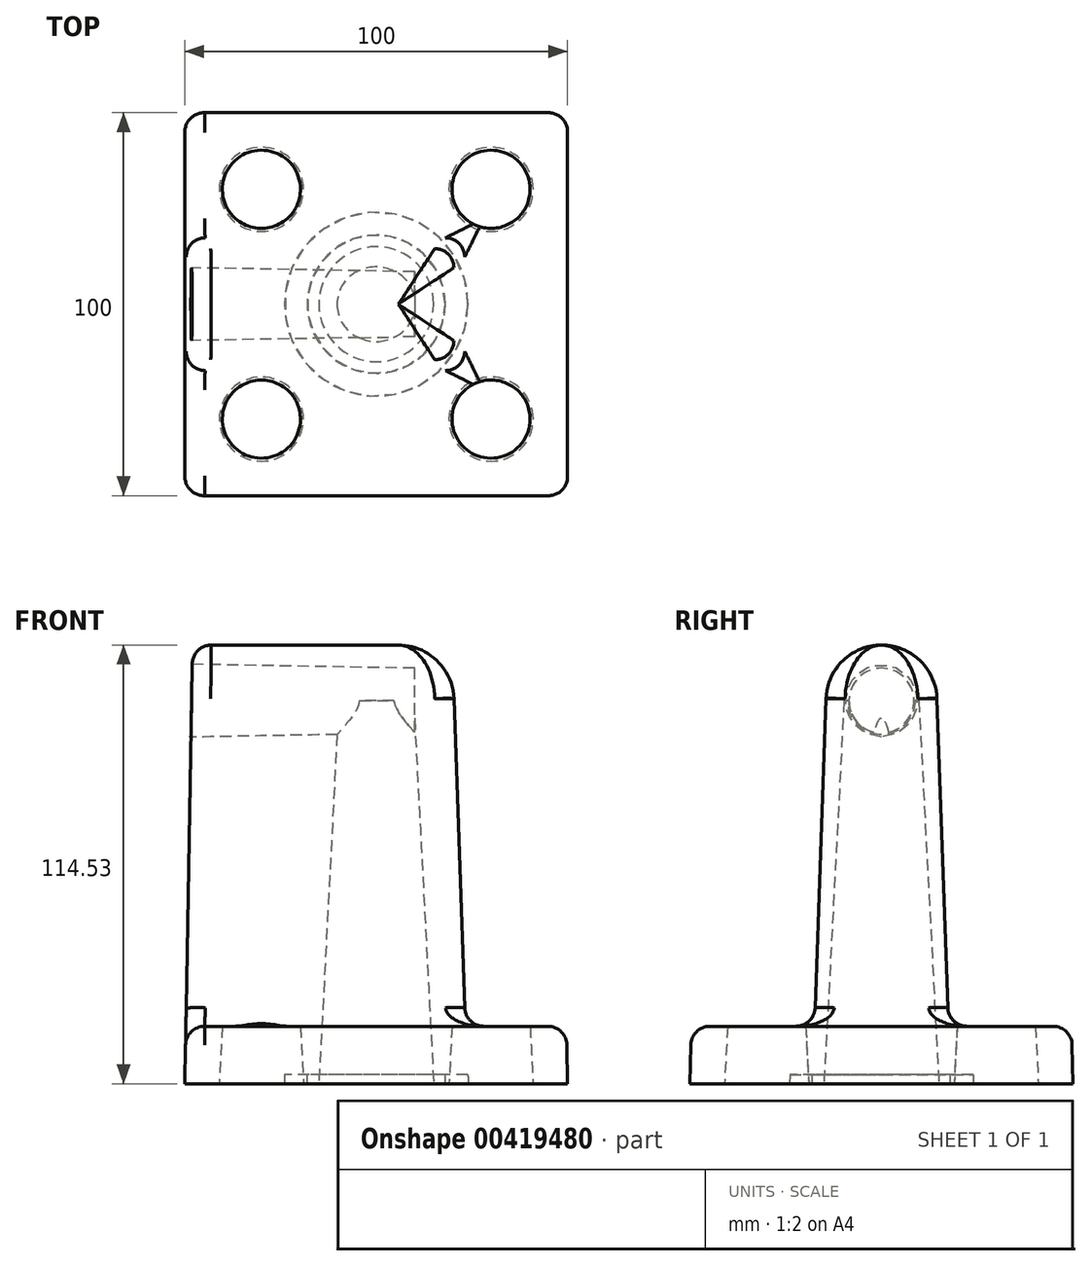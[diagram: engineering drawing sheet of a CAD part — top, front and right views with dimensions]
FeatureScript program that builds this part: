
annotation { "Feature Type Name" : "Feature", "Feature Type Description" : "" }
export const myFeature = defineFeature(function(context is Context, id is Id, definition is map)
    precondition{}
    {
        {
            var Q0;
            Q0=qCreatedBy(makeId("Top.planeOp"),FACE);
            var sketch = newSketch(context, id + "F0", { "sketchPlane" : qUnion([Q0])});
            skLineSegment(sketch, "E0.bottom", {"start": v(50, 50) * mm, "end": v(-50, 50) * mm});
            skLineSegment(sketch, "E0.top", {"start": v(50, -50) * mm, "end": v(-50, -50) * mm});
            skLineSegment(sketch, "E0.left", {"start": v(50, 50) * mm, "end": v(50, -50) * mm});
            skLineSegment(sketch, "E0.right", {"start": v(-50, 50) * mm, "end": v(-50, -50) * mm});
            skPoint(sketch, "E0.middle", {"position": v(0, 0) * mm});
            skCircle(sketch, "E1", {"center": v(-30, 30) * mm, "radius": 11 * mm});
            skCircle(sketch, "E2", {"center": v(30, 30) * mm, "radius": 11 * mm});
            skCircle(sketch, "E3", {"center": v(30, -30) * mm, "radius": 11 * mm});
            skCircle(sketch, "E4", {"center": v(-30, -30) * mm, "radius": 11 * mm});
            skCircle(sketch, "E5", {"center": v(0, 0) * mm, "radius": 15 * mm});
            skSolve(sketch);
        }
        {
            var Q0;
            Q0=makeQuery(id+"F0.imprint","IMPRINT",FACE,{"disambiguationData":[TD([[makeQuery(id+"F0.imprint","IMPRINT",EDGE,{"derivedFrom":sQuery(id+"F0.wireOp",EDGE,"E5")}),1.0]])]});
            var Q1;
            Q1=makeQuery(id+"F0.imprint","IMPRINT",FACE,{"disambiguationData":[TD([[makeQuery(id+"F0.imprint","IMPRINT",EDGE,{"derivedFrom":sQuery(id+"F0.wireOp",EDGE,"E0.bottom")}),1.0]])]});
            var Q2;
            Q2=makeQuery(id+"F0.imprint","IMPRINT",FACE,{"disambiguationData":[TD([[makeQuery(id+"F0.imprint","IMPRINT",EDGE,{"derivedFrom":sQuery(id+"F0.wireOp",EDGE,"E3")}),1.0]])]});
            var Q3;
            Q3=makeQuery(id+"F0.imprint","IMPRINT",FACE,{"disambiguationData":[TD([[makeQuery(id+"F0.imprint","IMPRINT",EDGE,{"derivedFrom":sQuery(id+"F0.wireOp",EDGE,"E4")}),1.0]])]});
            var Q4;
            Q4=makeQuery(id+"F0.imprint","IMPRINT",FACE,{"disambiguationData":[TD([[makeQuery(id+"F0.imprint","IMPRINT",EDGE,{"derivedFrom":sQuery(id+"F0.wireOp",EDGE,"E2")}),1.0]])]});
            var Q5;
            Q5=makeQuery(id+"F0.imprint","IMPRINT",FACE,{"disambiguationData":[TD([[makeQuery(id+"F0.imprint","IMPRINT",EDGE,{"derivedFrom":sQuery(id+"F0.wireOp",EDGE,"E1")}),1.0]])]});
            extrude(context, id + "F1", {"entities" : qUnion([Q0, Q1, Q2, Q3, Q4, Q5]), "depth" : 150 * mm, "hasDraft" : true, "draftAngle" : 1 * degree, "draftPullDirection" : true});
        }
        {
            var Q0;
            Q0=qCreatedBy(makeId("Right.planeOp"),FACE);
            var Q1;
            Q1=makeQuery(id+"F1.opExtrude","CAP_VERTEX",VERTEX,{"disambiguationData":[OSD([sQuery(id+"F0.wireOp",EDGE,"E0.top"),sQuery(id+"F0.wireOp",EDGE,"E0.right")])],"isStart":true});
            cPlane(context, id + "F2", {"entities" : qUnion([Q0, Q1]), "cplaneType" : CPlaneType.PLANE_POINT, "offset" : 25 * mm, "width" : 150 * mm, "height" : 150 * mm});
        }
        {
            var Q0;
            Q0=qCreatedBy(id+"F2.planeOp",FACE);
            var sketch = newSketch(context, id + "F3", { "sketchPlane" : qUnion([Q0])});
            skLineSegment(sketch, "E6", {"start": v(44.82, 15) * mm, "end": v(22.33, 15) * mm});
            skCircle(sketch, "E7", {"center": v(0, 100) * mm, "radius": 9.53 * mm});
            skArc(sketch, "E8", {"start": v(14.52, 100.5) * mm, "mid": v(10.09, 110.45) * mm, "end": v(0, 114.53) * mm});
            skLineSegment(sketch, "E9", {"start": v(14.52, 100.5) * mm, "end": v(17.33, 19.83) * mm});
            skLineSegment(sketch, "E10", {"start": v(0, 0) * mm, "end": v(0, 100) * mm, "construction": true});
            skLineSegment(sketch, "E11", {"start": v(49.82, 10.09) * mm, "end": v(50, 0) * mm});
            skLineSegment(sketch, "E12", {"start": v(50, 0) * mm, "end": v(65.53, 0) * mm});
            skLineSegment(sketch, "E13", {"start": v(65.53, 0) * mm, "end": v(56.35, 171.03) * mm});
            skLineSegment(sketch, "E14", {"start": v(56.35, 171.03) * mm, "end": v(0, 171.03) * mm});
            skPoint(sketch, "E15.visualSharp", {"position": v(17.5, 15) * mm});
            skArc(sketch, "E15.filletArc", {"start": v(17.33, 19.83) * mm, "mid": v(18.86, 16.4) * mm, "end": v(22.33, 15) * mm});
            skPoint(sketch, "E16.visualSharp", {"position": v(49.74, 15) * mm});
            skArc(sketch, "E16.filletArc", {"start": v(49.82, 10.09) * mm, "mid": v(48.33, 13.57) * mm, "end": v(44.82, 15) * mm});
            skArc(sketch, "E17.MirrorCS", {"start": v(-14.52, 100.5) * mm, "mid": v(-10.09, 110.45) * mm, "end": v(0, 114.53) * mm});
            skLineSegment(sketch, "E18.MirrorCS", {"start": v(-14.52, 100.5) * mm, "end": v(-17.33, 19.83) * mm});
            skArc(sketch, "E19.MirrorCS", {"start": v(-17.33, 19.83) * mm, "mid": v(-18.86, 16.4) * mm, "end": v(-22.33, 15) * mm});
            skLineSegment(sketch, "E20.MirrorCS", {"start": v(-44.82, 15) * mm, "end": v(-22.33, 15) * mm});
            skArc(sketch, "E21.MirrorCS", {"start": v(-49.82, 10.09) * mm, "mid": v(-48.33, 13.57) * mm, "end": v(-44.82, 15) * mm});
            skLineSegment(sketch, "E22.MirrorCS", {"start": v(-49.82, 10.09) * mm, "end": v(-50, 0) * mm});
            skLineSegment(sketch, "E23.MirrorCS", {"start": v(-50, 0) * mm, "end": v(-65.53, 0) * mm});
            skLineSegment(sketch, "E24.MirrorCS", {"start": v(-65.53, 0) * mm, "end": v(-56.35, 171.03) * mm});
            skLineSegment(sketch, "E25.MirrorCS", {"start": v(-56.35, 171.03) * mm, "end": v(0, 171.03) * mm});
            skSolve(sketch);
        }
        {
            var Q0;
            Q0=makeQuery(id+"F3.imprint","IMPRINT",FACE,{"disambiguationData":[TD([[makeQuery(id+"F3.imprint","IMPRINT",EDGE,{"derivedFrom":sQuery(id+"F3.wireOp",EDGE,"E6")}),-1.0]])]});
            extrude(context, id + "F4", {"entities" : qUnion([Q0]), "operationType" : NewBodyOperationType.REMOVE, "endBound" : BoundingType.THROUGH_ALL, "depth" : 25 * mm});
        }
        {
            var Q0;
            Q0=makeQuery(id+"F0.imprint","IMPRINT",FACE,{"disambiguationData":[TD([[makeQuery(id+"F0.imprint","IMPRINT",EDGE,{"derivedFrom":sQuery(id+"F0.wireOp",EDGE,"E5")}),1.0]])]});
            var Q1;
            Q1=makeQuery(id+"F0.imprint","IMPRINT",FACE,{"disambiguationData":[TD([[makeQuery(id+"F0.imprint","IMPRINT",EDGE,{"derivedFrom":sQuery(id+"F0.wireOp",EDGE,"E4")}),1.0]])]});
            var Q2;
            Q2=makeQuery(id+"F0.imprint","IMPRINT",FACE,{"disambiguationData":[TD([[makeQuery(id+"F0.imprint","IMPRINT",EDGE,{"derivedFrom":sQuery(id+"F0.wireOp",EDGE,"E3")}),1.0]])]});
            var Q3;
            Q3=makeQuery(id+"F0.imprint","IMPRINT",FACE,{"disambiguationData":[TD([[makeQuery(id+"F0.imprint","IMPRINT",EDGE,{"derivedFrom":sQuery(id+"F0.wireOp",EDGE,"E2")}),1.0]])]});
            var Q4;
            Q4=makeQuery(id+"F0.imprint","IMPRINT",FACE,{"disambiguationData":[TD([[makeQuery(id+"F0.imprint","IMPRINT",EDGE,{"derivedFrom":sQuery(id+"F0.wireOp",EDGE,"E1")}),1.0]])]});
            extrude(context, id + "F5", {"entities" : qUnion([Q0, Q1, Q2, Q3, Q4]), "operationType" : NewBodyOperationType.REMOVE, "depth" : 100 * mm, "hasDraft" : true, "draftAngle" : 3 * degree, "draftPullDirection" : true});
        }
        {
            var Q0;
            Q0=makeQuery(id+"F3.imprint","IMPRINT",FACE,{"disambiguationData":[TD([[makeQuery(id+"F3.imprint","IMPRINT",EDGE,{"derivedFrom":sQuery(id+"F3.wireOp",EDGE,"E7")}),1.0]])]});
            extrude(context, id + "F6", {"entities" : qUnion([Q0]), "operationType" : NewBodyOperationType.REMOVE, "depth" : 60 * mm, "hasDraft" : true, "draftAngle" : 1 * degree, "draftPullDirection" : true});
        }
        {
            var Q0;
            Q0=qCreatedBy(makeId("Front.planeOp"),FACE);
            var sketch = newSketch(context, id + "F7", { "sketchPlane" : qUnion([Q0])});
            skLineSegment(sketch, "E26", {"start": v(50, 0) * mm, "end": v(49.82, 10.09) * mm});
            skLineSegment(sketch, "E27", {"start": v(44.82, 15) * mm, "end": v(28.1, 15) * mm});
            skLineSegment(sketch, "E28", {"start": v(23.1, 19.83) * mm, "end": v(20.28, 100.53) * mm});
            skLineSegment(sketch, "E29", {"start": v(5.8, 114.53) * mm, "end": v(-54.15, 114.53) * mm});
            skLineSegment(sketch, "E30", {"start": v(-54.15, 114.53) * mm, "end": v(-54.15, 135.79) * mm});
            skLineSegment(sketch, "E31", {"start": v(-54.15, 135.79) * mm, "end": v(70.57, 135.79) * mm});
            skLineSegment(sketch, "E32", {"start": v(70.57, 135.79) * mm, "end": v(70.57, 0) * mm});
            skLineSegment(sketch, "E33", {"start": v(70.57, 0) * mm, "end": v(50, 0) * mm});
            skPoint(sketch, "E34.visualSharp", {"position": v(19.8, 114.53) * mm});
            skArc(sketch, "E34.filletArc", {"start": v(20.28, 100.53) * mm, "mid": v(15.86, 110.46) * mm, "end": v(5.8, 114.53) * mm});
            skPoint(sketch, "E35.visualSharp", {"position": v(23.27, 15) * mm});
            skArc(sketch, "E35.filletArc", {"start": v(23.1, 19.83) * mm, "mid": v(24.63, 16.4) * mm, "end": v(28.1, 15) * mm});
            skPoint(sketch, "E36.visualSharp", {"position": v(49.74, 15) * mm});
            skArc(sketch, "E36.filletArc", {"start": v(49.82, 10.09) * mm, "mid": v(48.33, 13.57) * mm, "end": v(44.82, 15) * mm});
            skSolve(sketch);
        }
        {
            var Q0;
            Q0 = qSketchRegion(id + "F7", true);
            extrude(context, id + "F8", {"entities" : qUnion([Q0]), "operationType" : NewBodyOperationType.REMOVE, "endBound" : BoundingType.THROUGH_ALL, "oppositeDirection" : true, "depth" : 25 * mm, "hasSecondDirection" : true, "secondDirectionBound" : SecondDirectionBoundingType.THROUGH_ALL, "secondDirectionOppositeDirection" : false, "secondDirectionDepth" : 25 * mm});
        }
        {
            var Q0;
            Q0=qCreatedBy(makeId("Front.planeOp"),FACE);
            var sketch = newSketch(context, id + "F9", { "sketchPlane" : qUnion([Q0])});
            skLineSegment(sketch, "E37", {"start": v(0, -11.4) * mm, "end": v(0, 11.28) * mm, "construction": true});
            skLineSegment(sketch, "E38.bottom", {"start": v(-24, 0) * mm, "end": v(-18, 0) * mm});
            skLineSegment(sketch, "E38.top", {"start": v(-23.96, 2.4) * mm, "end": v(-18.04, 2.4) * mm});
            skLineSegment(sketch, "E38.left", {"start": v(-24, 0) * mm, "end": v(-23.96, 2.4) * mm});
            skLineSegment(sketch, "E39", {"start": v(-18, 0) * mm, "end": v(-18.04, 2.4) * mm});
            skSolve(sketch);
        }
        {
            var Q0;
            Q0 = qSketchRegion(id + "F9", true);
            var Q1;
            Q1=sQuery(id+"F9.wireOp",EDGE,"E38.top");
            var Q2;
            Q2=sQuery(id+"F9.wireOp",EDGE,"E37");
            revolve(context, id + "F10", {"operationType" : NewBodyOperationType.REMOVE, "entities" : qUnion([Q0]), "surfaceEntities" : qUnion([Q1]), "axis" : qUnion([Q2]), "revolveType" : RevolveType.FULL, "oppositeDirection" : true});
        }
        {
            var Q0;
            Q0=makeQuery(id+"F4.boolean.opBoolean","INTERSECT",EDGE,{"derivedFrom":[makeQuery(id+"F1.opExtrude","SWEPT_FACE",FACE,{"disambiguationData":[OSD([sQuery(id+"F0.wireOp",EDGE,"E0.right")])]}),makeQuery(id+"F4.opExtrude","SWEPT_FACE",FACE,{"disambiguationData":[OSD([sQuery(id+"F3.wireOp",EDGE,"E6")])]})]});
            var Q1;
            Q1=makeQuery(id+"F8.boolean.opBoolean","INTERSECT",EDGE,{"derivedFrom":[makeQuery(id+"F4.boolean.opBoolean","COPY",FACE,{"derivedFrom":makeQuery(id+"F4.opExtrude","SWEPT_FACE",FACE,{"disambiguationData":[OSD([sQuery(id+"F3.wireOp",EDGE,"E18.MirrorCS")])]})}),makeQuery(id+"F8.opExtrude","SWEPT_FACE",FACE,{"disambiguationData":[OSD([sQuery(id+"F7.wireOp",EDGE,"E28")])]})]});
            var Q2;
            Q2=makeQuery(id+"F8.boolean.opBoolean","INTERSECT",EDGE,{"derivedFrom":[makeQuery(id+"F4.boolean.opBoolean","COPY",FACE,{"derivedFrom":makeQuery(id+"F4.opExtrude","SWEPT_FACE",FACE,{"disambiguationData":[OSD([sQuery(id+"F3.wireOp",EDGE,"E9")])]})}),makeQuery(id+"F8.opExtrude","SWEPT_FACE",FACE,{"disambiguationData":[OSD([sQuery(id+"F7.wireOp",EDGE,"E28")])]})]});
            var Q3;
            Q3=makeQuery(id+"F1.opExtrude","SWEPT_EDGE",EDGE,{"disambiguationData":[OSD([sQuery(id+"F0.wireOp",EDGE,"E0.bottom"),sQuery(id+"F0.wireOp",EDGE,"E0.left")])]});
            var Q4;
            Q4=makeQuery(id+"F1.opExtrude","SWEPT_EDGE",EDGE,{"disambiguationData":[OSD([sQuery(id+"F0.wireOp",EDGE,"E0.top"),sQuery(id+"F0.wireOp",EDGE,"E0.left")])]});
            fillet(context, id + "F11", {"entities" : qUnion([Q0, Q1, Q2, Q3, Q4]), "radius" : 5 * mm, "tangentPropagation" : true, "allowEdgeOverflow" : false});
        }
    });
